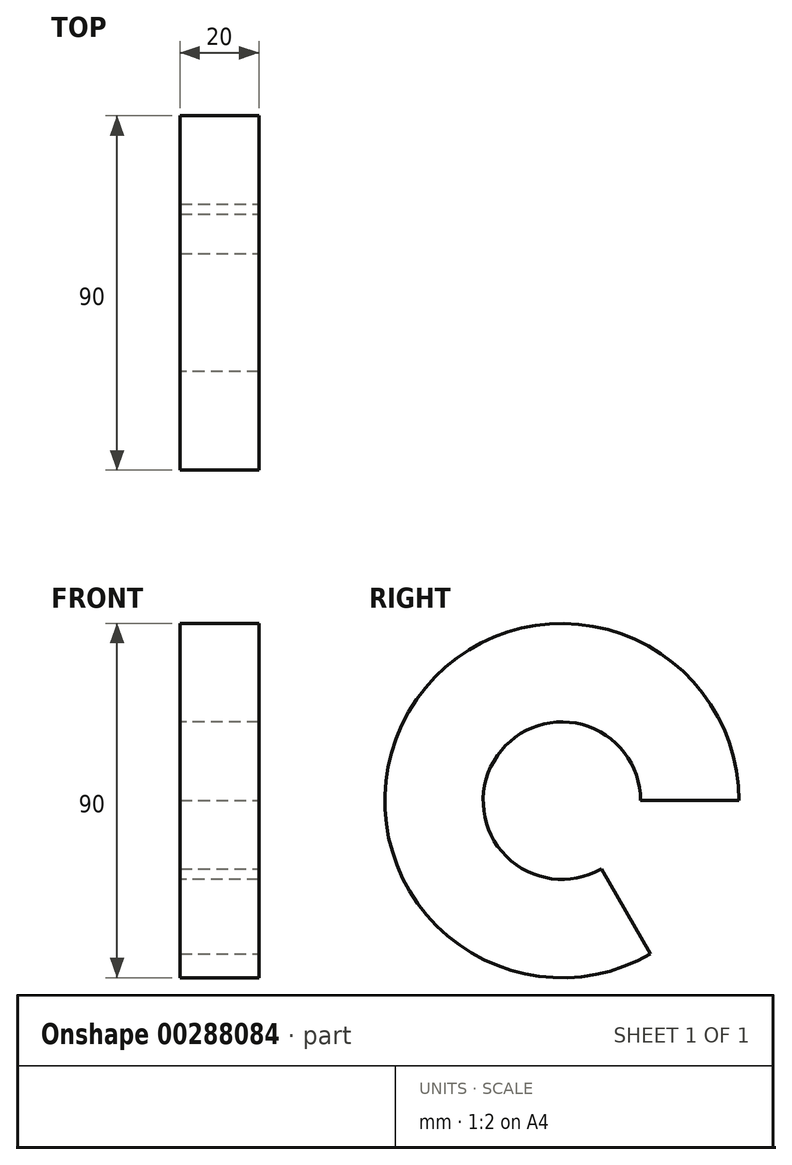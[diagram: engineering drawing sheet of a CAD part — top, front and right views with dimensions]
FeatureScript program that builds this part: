
annotation { "Feature Type Name" : "Feature", "Feature Type Description" : "" }
export const myFeature = defineFeature(function(context is Context, id is Id, definition is map)
    precondition{}
    {
        {
            var Q0;
            Q0=qCreatedBy(makeId("Top.planeOp"),FACE);
            var sketch = newSketch(context, id + "F0", { "sketchPlane" : qUnion([Q0])});
            skLineSegment(sketch, "E0.bottom", {"start": v(-10, 20) * mm, "end": v(10, 20) * mm});
            skLineSegment(sketch, "E0.top", {"start": v(-10, 45) * mm, "end": v(10, 45) * mm});
            skLineSegment(sketch, "E0.left", {"start": v(-10, 20) * mm, "end": v(-10, 45) * mm});
            skLineSegment(sketch, "E0.right", {"start": v(10, 20) * mm, "end": v(10, 45) * mm});
            skLineSegment(sketch, "E1", {"start": v(0, 0) * mm, "end": v(0, 20) * mm, "construction": true});
            skLineSegment(sketch, "E2", {"start": v(0, 0) * mm, "end": v(10, 0) * mm, "construction": true});
            skSolve(sketch);
        }
        {
            var Q0;
            Q0 = qSketchRegion(id + "F0", true);
            var Q1;
            Q1=sQuery(id+"F0.wireOp",EDGE,"E2");
            revolve(context, id + "F1", {"entities" : qUnion([Q0]), "axis" : qUnion([Q1]), "revolveType" : RevolveType.ONE_DIRECTION, "angle" : 300 * degree});
        }
    });
